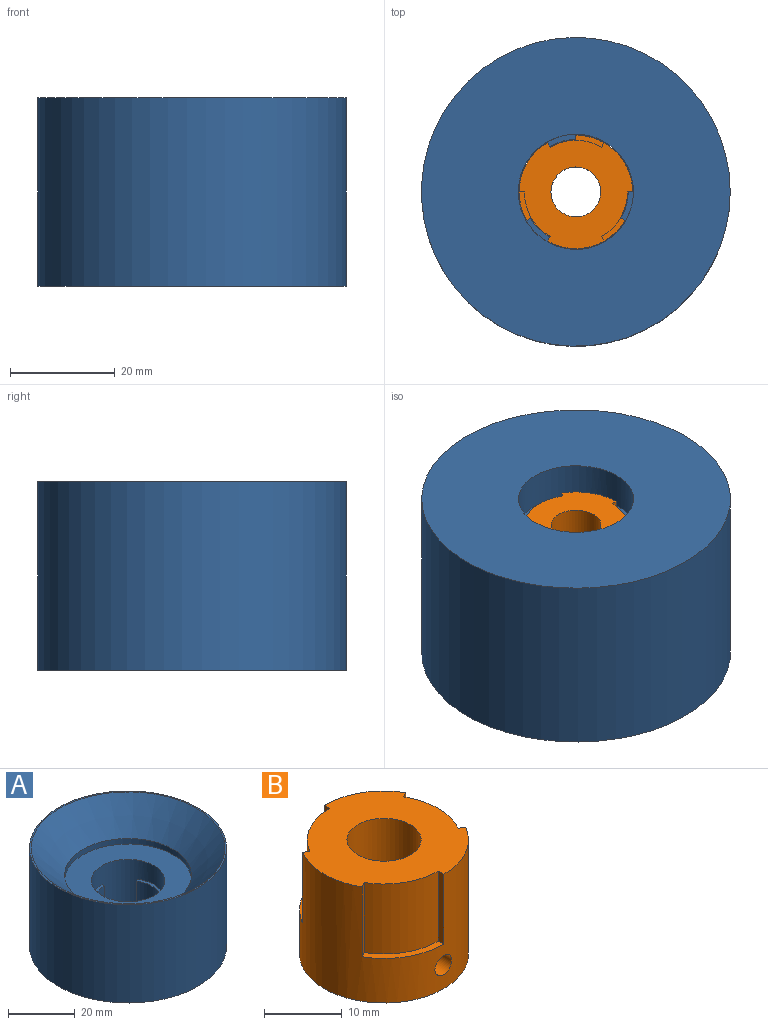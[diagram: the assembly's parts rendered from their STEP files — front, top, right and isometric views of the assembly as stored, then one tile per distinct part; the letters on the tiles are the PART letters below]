
ASSEMBLY  parts=2 mates=1
PART A: 22 faces, bbox 59x59x36 mm
  f0: plane 10x1mm, normal (1,0,0), area 10mm2, adj f1,f9,f14,f17
  f1: cylinder r=10mm len=10mm, axis (0,0,-1), area 104.7mm2, adj f0,f2,f14,f17
  f2: plane 10x0.87mm, normal (-0.5,0.87,0), area 10mm2, adj f1,f9,f14,f17
  f3: plane 10x0.87mm, normal (-0.5,-0.87,0), area 10mm2, adj f4,f9,f13,f16
  f4: cylinder r=10mm len=10mm, axis (0,0,-1), area 104.7mm2, adj f3,f5,f13,f16
  f5: plane 10x1mm, normal (1,0,0), area 10mm2, adj f4,f9,f13,f16
  f6: plane 10x0.87mm, normal (-0.5,0.87,0), area 10mm2, adj f7,f9,f12,f15
  f7: cylinder r=10mm len=10mm, axis (0,0,-1), area 104.7mm2, adj f6,f8,f12,f15
  f8: plane 10x0.87mm, normal (-0.5,-0.87,0), area 10mm2, adj f7,f9,f12,f15
  f9: cylinder r=11mm len=24mm, axis (0,0,-1), area 1313.2mm2, adj f0,f2,f3,f5,f6,f8,f10,f11
  f10: plane 38x38mm, normal (0,0,1), area 754mm2, adj f9,f18
  f11: plane 59x59mm, normal (0,0,-1), area 2353.8mm2, adj f9,f19
  f12: plane 11x2.34mm, normal (0,0,-1), area 11mm2, adj f6,f7,f8,f9
  f13: plane 9.53x6mm, normal (0,0,-1), area 11mm2, adj f3,f4,f5,f9
  f14: plane 9.53x6mm, normal (0,0,-1), area 11mm2, adj f0,f1,f2,f9
  f15: plane 11x2.34mm, normal (0,0,1), area 11mm2, adj f6,f7,f8,f9
  f16: plane 9.53x6mm, normal (0,0,1), area 11mm2, adj f3,f4,f5,f9
  f17: plane 9.53x6mm, normal (0,0,1), area 11mm2, adj f0,f1,f2,f9
  f18: cylinder r=19mm len=38mm, axis (0,0,-1), area 238.8mm2, adj f10,f21
  f19: cylinder r=29.5mm len=59mm, axis (0,0,-1), area 6672.7mm2, adj f11,f20
  f20: plane 59x59mm, normal (0,0,1), area 91.9mm2, adj f19,f21
  f21: cone r=19mm half-angle=45deg, axis (0,0,1), area 2132.6mm2, adj f18,f20
PART B: 18 faces, bbox 21.7x21.7x18 mm
  f0: plane 11x0.87mm, normal (0.5,-0.87,0), area 11mm2, adj f1,f10,f11,f15
  f1: cylinder r=9.85mm len=11mm, axis (0,0,-1), area 113.5mm2, adj f0,f2,f11,f15
  f2: plane 11x1mm, normal (-1,0,0), area 11mm2, adj f1,f10,f11,f15
  f3: plane 11x0.87mm, normal (0.5,0.87,0), area 11mm2, adj f4,f10,f11,f14
  f4: cylinder r=9.85mm len=11mm, axis (0,0,-1), area 113.5mm2, adj f3,f5,f11,f14
  f5: plane 11x0.87mm, normal (0.5,-0.87,0), area 11mm2, adj f4,f10,f11,f14
  f6: plane 11x1mm, normal (-1,0,0), area 11mm2, adj f7,f10,f11,f13
  f7: cylinder r=9.85mm len=11mm, axis (0,0,-1), area 113.5mm2, adj f6,f8,f11,f13
  f8: plane 11x0.87mm, normal (0.5,0.87,0), area 11mm2, adj f7,f10,f11,f13
  f9: cylinder r=4.76mm len=18mm, axis (0,0,-1), area 524.3mm2, adj f11,f12,f16,f17
  f10: cylinder r=10.85mm len=21.7mm, axis (0,0,-1), area 837.9mm2, adj f0,f2,f3,f5,f6,f8,f11,f12
  f11: plane 21.7x20.7mm, normal (0,0,1), area 266.1mm2, adj f0,f1,f2,f3,f4,f5,f6,f7
  f12: plane 21.7x21.7mm, normal (0,0,-1), area 298.6mm2, adj f9,f10
  f13: plane 9.4x5.93mm, normal (0,0,1), area 10.8mm2, adj f6,f7,f8,f10
  f14: plane 10.85x2.32mm, normal (0,0,1), area 10.8mm2, adj f3,f4,f5,f10
  f15: plane 9.4x5.93mm, normal (0,0,1), area 10.8mm2, adj f0,f1,f2,f10
  f16: cylinder r=1.5mm len=6.33mm, axis (0,-1,0), area 58mm2, adj f9,f10
  f17: cylinder r=1.5mm len=6.33mm, axis (0,-1,0), area 58mm2, adj f9,f10
PLACE A rot(axis=(1,0,0),180deg) t=(0,0,30)mm
PLACE B rot(axis=(0,0,1),90deg) t=(0,0,6)mm
MATE cylindrical B.f9 <-> A.f1  axis (0,0,-1) through (0,0,6)mm
